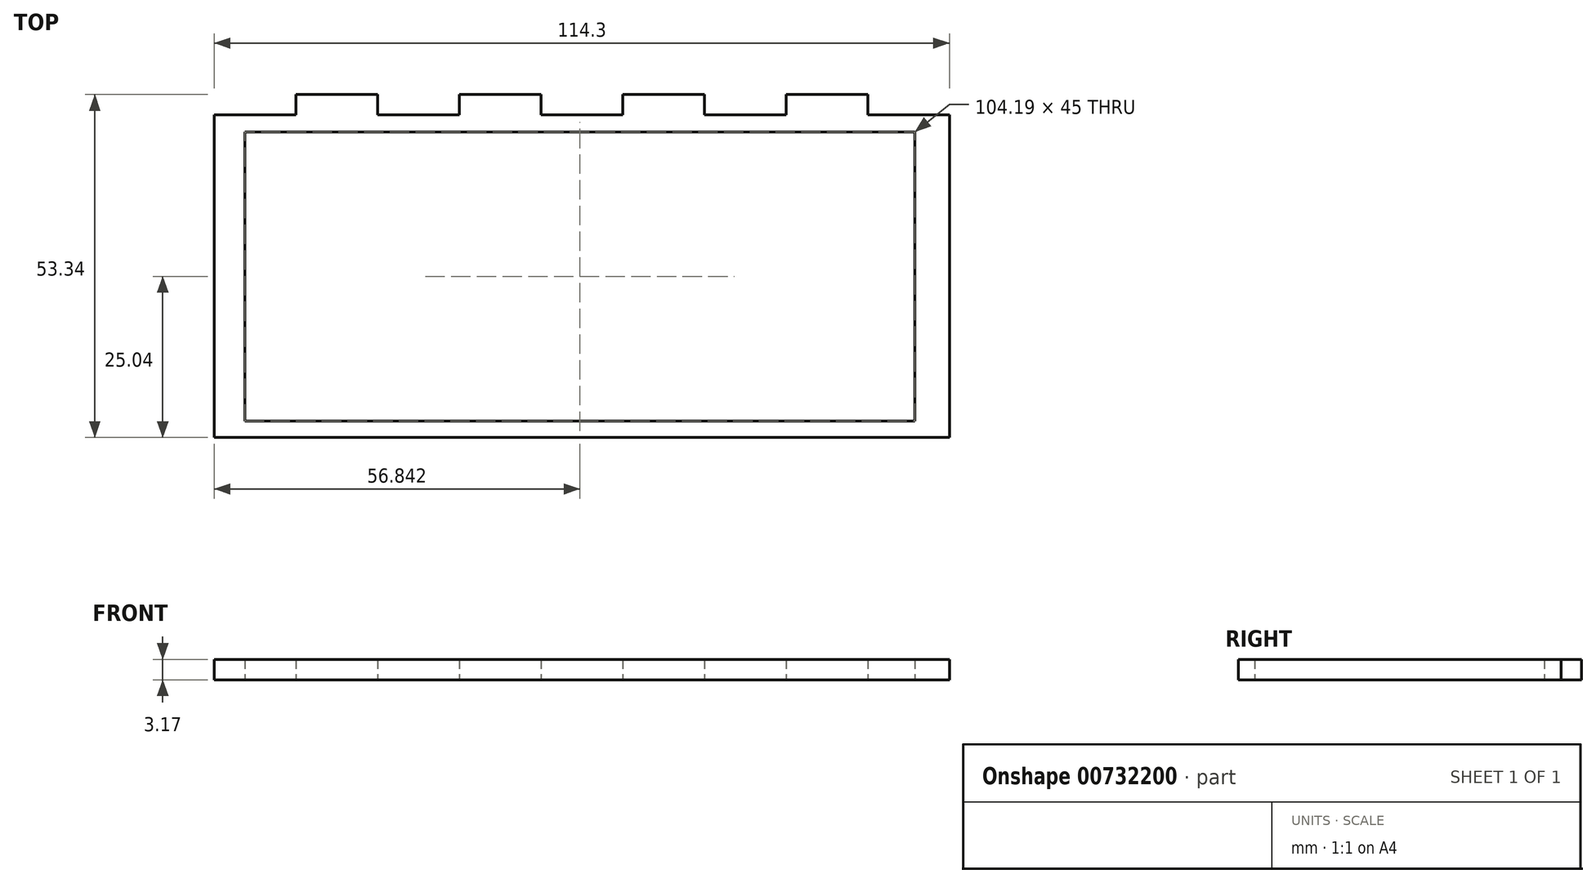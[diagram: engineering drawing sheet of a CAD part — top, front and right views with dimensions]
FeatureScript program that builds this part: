
annotation { "Feature Type Name" : "Feature", "Feature Type Description" : "" }
export const myFeature = defineFeature(function(context is Context, id is Id, definition is map)
    precondition{}
    {
        {
            var Q0;
            Q0=qCreatedBy(makeId("Top.planeOp"),FACE);
            var sketch = newSketch(context, id + "F0", { "sketchPlane" : qUnion([Q0])});
            skLineSegment(sketch, "E0.bottom", {"start": v(-88.05, 50.8) * mm, "end": v(64.35, 50.8) * mm});
            skLineSegment(sketch, "E0.top", {"start": v(-88.05, -25.4) * mm, "end": v(64.35, -25.4) * mm});
            skLineSegment(sketch, "E0.left", {"start": v(-88.05, 50.8) * mm, "end": v(-88.05, -25.4) * mm});
            skLineSegment(sketch, "E0.right", {"start": v(64.35, 50.8) * mm, "end": v(64.35, -25.4) * mm});
            skLineSegment(sketch, "E1", {"start": v(-11.85, -25.4) * mm, "end": v(-11.85, -76.2) * mm});
            skLineSegment(sketch, "E2", {"start": v(-11.85, -76.2) * mm, "end": v(-43.6, -76.2) * mm});
            skLineSegment(sketch, "E3", {"start": v(-43.6, -76.2) * mm, "end": v(-43.6, -25.4) * mm});
            skLineSegment(sketch, "E4", {"start": v(-11.85, -76.2) * mm, "end": v(19.9, -76.2) * mm});
            skLineSegment(sketch, "E5", {"start": v(19.9, -76.2) * mm, "end": v(19.9, -25.4) * mm});
            skLineSegment(sketch, "E6", {"start": v(-88.05, -25.4) * mm, "end": v(-88.05, -19.05) * mm});
            skLineSegment(sketch, "E7", {"start": v(-88.05, -19.05) * mm, "end": v(-84.87, -19.05) * mm});
            skLineSegment(sketch, "E8", {"start": v(-84.87, -19.05) * mm, "end": v(-84.87, 44.45) * mm});
            skLineSegment(sketch, "E9", {"start": v(-84.87, 44.45) * mm, "end": v(-88.05, 44.45) * mm});
            skLineSegment(sketch, "E10.MirrorCS", {"start": v(64.35, -19.05) * mm, "end": v(61.18, -19.05) * mm});
            skLineSegment(sketch, "E11.MirrorCS", {"start": v(61.18, -19.05) * mm, "end": v(61.18, 44.45) * mm});
            skLineSegment(sketch, "E12.MirrorCS", {"start": v(61.18, 44.45) * mm, "end": v(64.35, 44.45) * mm});
            skLineSegment(sketch, "E13", {"start": v(64.35, 50.8) * mm, "end": v(58, 50.8) * mm});
            skLineSegment(sketch, "E14", {"start": v(58, 50.8) * mm, "end": v(58, 47.62) * mm});
            skLineSegment(sketch, "E15", {"start": v(58, 47.62) * mm, "end": v(-81.7, 47.62) * mm});
            skLineSegment(sketch, "E16", {"start": v(-81.7, 47.62) * mm, "end": v(-81.7, 50.8) * mm});
            skLineSegment(sketch, "E17", {"start": v(-84.87, 44.45) * mm, "end": v(-84.87, 31.75) * mm});
            skLineSegment(sketch, "E18", {"start": v(-84.87, 31.75) * mm, "end": v(-88.05, 31.75) * mm});
            skLineSegment(sketch, "E19", {"start": v(-88.05, 31.75) * mm, "end": v(-88.05, 19.05) * mm});
            skLineSegment(sketch, "E20", {"start": v(-88.05, 19.05) * mm, "end": v(-84.87, 19.05) * mm});
            skLineSegment(sketch, "E21", {"start": v(-84.87, 19.05) * mm, "end": v(-84.87, 6.35) * mm});
            skLineSegment(sketch, "E22", {"start": v(-84.87, 6.35) * mm, "end": v(-88.05, 6.35) * mm});
            skLineSegment(sketch, "E23", {"start": v(-88.05, 6.35) * mm, "end": v(-88.05, -6.35) * mm});
            skLineSegment(sketch, "E24", {"start": v(-88.05, -6.35) * mm, "end": v(-84.87, -6.35) * mm});
            skLineSegment(sketch, "E25.MirrorCS", {"start": v(64.35, -6.35) * mm, "end": v(61.18, -6.35) * mm});
            skLineSegment(sketch, "E26.MirrorCS", {"start": v(61.18, 6.35) * mm, "end": v(64.35, 6.35) * mm});
            skLineSegment(sketch, "E27.MirrorCS", {"start": v(64.35, 19.05) * mm, "end": v(61.18, 19.05) * mm});
            skLineSegment(sketch, "E28.MirrorCS", {"start": v(61.18, 31.75) * mm, "end": v(64.35, 31.75) * mm});
            skLineSegment(sketch, "E29", {"start": v(-81.7, 47.62) * mm, "end": v(-56.3, 47.62) * mm});
            skLineSegment(sketch, "E30", {"start": v(-56.3, 47.62) * mm, "end": v(-56.3, 50.8) * mm});
            skLineSegment(sketch, "E31", {"start": v(-56.3, 50.8) * mm, "end": v(-30.9, 50.8) * mm});
            skLineSegment(sketch, "E32", {"start": v(-30.9, 50.8) * mm, "end": v(-30.9, 47.62) * mm});
            skLineSegment(sketch, "E33", {"start": v(-30.9, 47.62) * mm, "end": v(-18.2, 47.62) * mm});
            skLineSegment(sketch, "E34", {"start": v(-18.2, 47.62) * mm, "end": v(-18.2, 50.8) * mm});
            skLineSegment(sketch, "E35", {"start": v(-18.2, 50.8) * mm, "end": v(-5.5, 50.8) * mm});
            skLineSegment(sketch, "E36", {"start": v(-5.5, 50.8) * mm, "end": v(-5.5, 47.62) * mm});
            skLineSegment(sketch, "E37", {"start": v(-5.5, 47.62) * mm, "end": v(7.2, 47.62) * mm});
            skLineSegment(sketch, "E38", {"start": v(7.2, 47.62) * mm, "end": v(7.2, 50.8) * mm});
            skLineSegment(sketch, "E39", {"start": v(7.2, 50.8) * mm, "end": v(32.6, 50.8) * mm});
            skLineSegment(sketch, "E40", {"start": v(32.6, 50.8) * mm, "end": v(32.6, 47.62) * mm});
            skLineSegment(sketch, "E41", {"start": v(-43.6, 50.8) * mm, "end": v(-43.6, 47.62) * mm});
            skLineSegment(sketch, "E42", {"start": v(-69, 47.62) * mm, "end": v(-69, 50.8) * mm});
            skLineSegment(sketch, "E43", {"start": v(19.9, 50.8) * mm, "end": v(19.9, 47.62) * mm});
            skLineSegment(sketch, "E44", {"start": v(58, 47.62) * mm, "end": v(45.3, 47.62) * mm});
            skLineSegment(sketch, "E45", {"start": v(45.3, 47.62) * mm, "end": v(45.3, 50.8) * mm});
            skLineSegment(sketch, "E46", {"start": v(-88.05, -25.4) * mm, "end": v(-88.05, -63.5) * mm});
            skLineSegment(sketch, "E47", {"start": v(-88.05, -63.5) * mm, "end": v(-69, -63.5) * mm});
            skLineSegment(sketch, "E48", {"start": v(-69, -63.5) * mm, "end": v(-69, -25.4) * mm});
            skLineSegment(sketch, "E49", {"start": v(64.35, -25.4) * mm, "end": v(64.35, -63.5) * mm});
            skLineSegment(sketch, "E50", {"start": v(64.35, -63.5) * mm, "end": v(45.3, -63.5) * mm});
            skLineSegment(sketch, "E51", {"start": v(45.3, -63.5) * mm, "end": v(45.3, -25.4) * mm});
            skLineSegment(sketch, "E52", {"start": v(-11.85, -25.4) * mm, "end": v(-11.85, 0) * mm});
            skLineSegment(sketch, "E53", {"start": v(-11.85, 0) * mm, "end": v(39.94, 0) * mm});
            skLineSegment(sketch, "E54", {"start": v(39.94, 0) * mm, "end": v(39.94, 45) * mm});
            skLineSegment(sketch, "E55", {"start": v(39.94, 45) * mm, "end": v(-64.25, 45) * mm});
            skLineSegment(sketch, "E56", {"start": v(-64.25, 45) * mm, "end": v(-64.25, 0) * mm});
            skLineSegment(sketch, "E57", {"start": v(-64.25, 0) * mm, "end": v(-11.85, 0) * mm});
            skLineSegment(sketch, "E58", {"start": v(-69, 47.62) * mm, "end": v(-69, 0) * mm});
            skLineSegment(sketch, "E59", {"start": v(-69, 0) * mm, "end": v(-69, -2.54) * mm});
            skLineSegment(sketch, "E60.MirrorCS", {"start": v(45.3, 47.62) * mm, "end": v(45.3, 0) * mm});
            skLineSegment(sketch, "E61.MirrorCS", {"start": v(45.3, 0) * mm, "end": v(45.3, -2.54) * mm});
            skLineSegment(sketch, "E62", {"start": v(-69, -2.54) * mm, "end": v(45.3, -2.54) * mm});
            skSolve(sketch);
        }
        {
            var Q0;
            Q0=makeQuery(id+"F0.imprint","IMPRINT",FACE,{"disambiguationData":[TD([[makeQuery(id+"F0.imprint","IMPRINT",EDGE,{"derivedFrom":sQuery(id+"F0.wireOp",EDGE,"E53")}),-1.0]])]});
            var Q1;
            {var subQ0=sQuery(id+"F0.wireOp",EDGE,"E30");Q1=makeQuery(id+"F0.imprint","IMPRINT",FACE,{"disambiguationData":[TD([[makeQuery(id+"F0.imprint","IMPRINT",EDGE,{"derivedFrom":subQ0}),-1.0]])]});}
            var Q2;
            {var subQ0=sQuery(id+"F0.wireOp",EDGE,"E32");Q2=makeQuery(id+"F0.imprint","IMPRINT",FACE,{"disambiguationData":[TD([[makeQuery(id+"F0.imprint","IMPRINT",EDGE,{"derivedFrom":subQ0}),1.0]])]});}
            var Q3;
            {var subQ0=sQuery(id+"F0.wireOp",EDGE,"E36");Q3=makeQuery(id+"F0.imprint","IMPRINT",FACE,{"disambiguationData":[TD([[makeQuery(id+"F0.imprint","IMPRINT",EDGE,{"derivedFrom":subQ0}),1.0]])]});}
            var Q4;
            {var subQ0=sQuery(id+"F0.wireOp",EDGE,"E40");Q4=makeQuery(id+"F0.imprint","IMPRINT",FACE,{"disambiguationData":[TD([[makeQuery(id+"F0.imprint","IMPRINT",EDGE,{"derivedFrom":subQ0}),-1.0]])]});}
            extrude(context, id + "F1", {"entities" : qUnion([Q0, Q1, Q2, Q3, Q4]), "depth" : 3.17 * mm, "offsetDistance" : 25.4 * mm});
        }
    });
